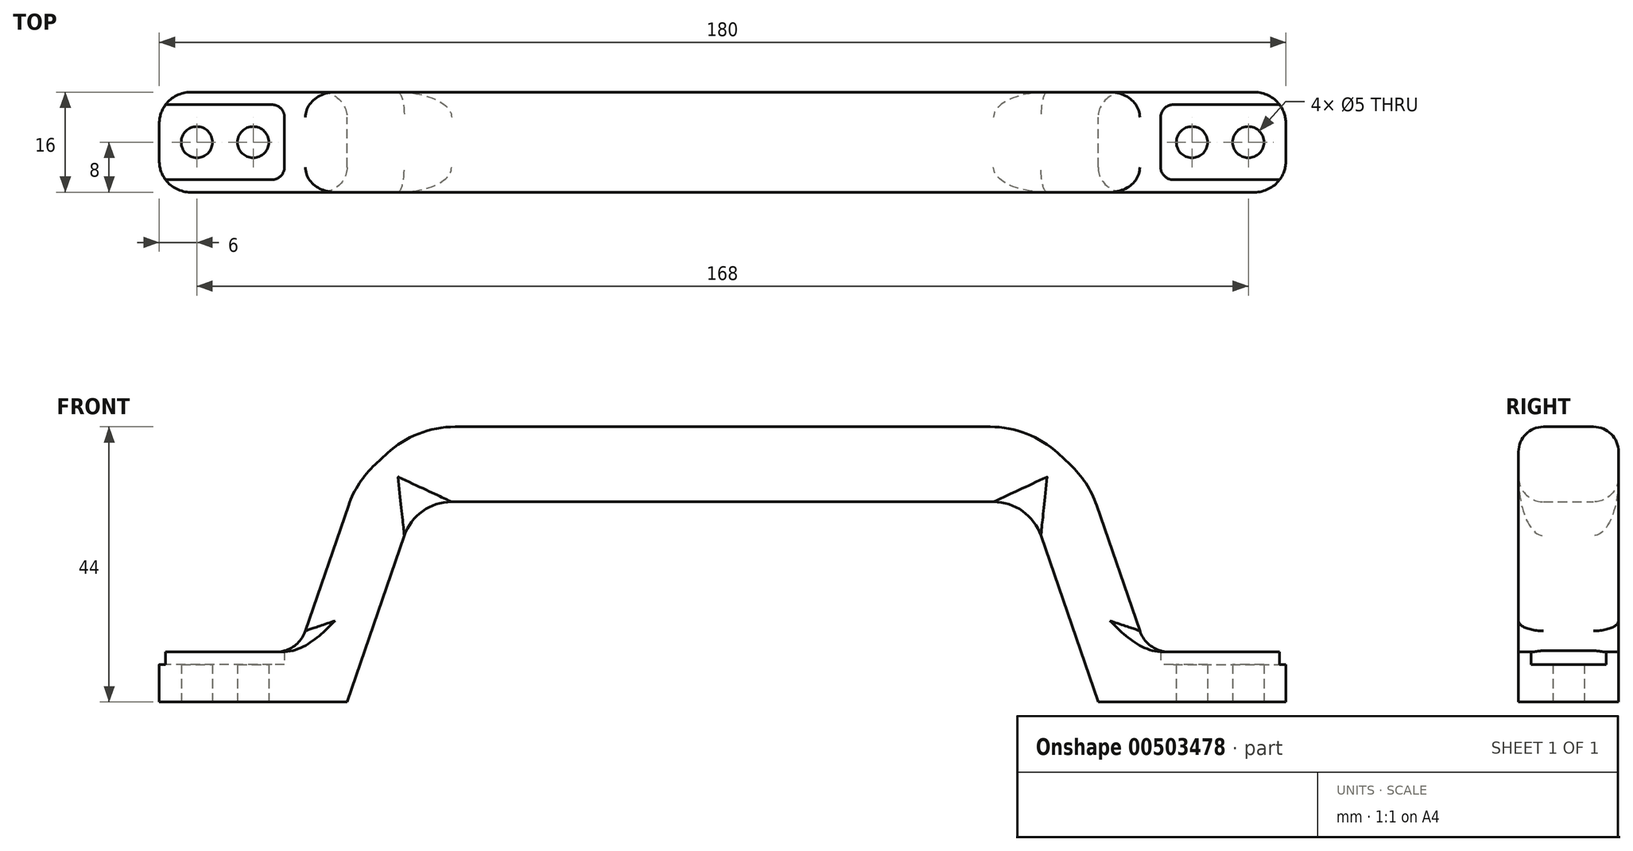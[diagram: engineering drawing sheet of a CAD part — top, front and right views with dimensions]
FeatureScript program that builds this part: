
annotation { "Feature Type Name" : "Feature", "Feature Type Description" : "" }
export const myFeature = defineFeature(function(context is Context, id is Id, definition is map)
    precondition{}
    {
        {
            var Q0;
            Q0=qCreatedBy(makeId("Front.planeOp"),FACE);
            var sketch = newSketch(context, id + "F0", { "sketchPlane" : qUnion([Q0])});
            skLineSegment(sketch, "E0", {"start": v(-60, 0) * mm, "end": v(-90, 0) * mm});
            skLineSegment(sketch, "E1", {"start": v(-90, 0) * mm, "end": v(-90, 8) * mm});
            skLineSegment(sketch, "E2", {"start": v(-90, 8) * mm, "end": v(-67.82, 8) * mm});
            skLineSegment(sketch, "E3", {"start": v(0, 0) * mm, "end": v(0, 32) * mm});
            skLineSegment(sketch, "E4", {"start": v(0, 32) * mm, "end": v(-49, 32) * mm});
            skLineSegment(sketch, "E5", {"start": v(-49, 32) * mm, "end": v(-60, 0) * mm});
            skLineSegment(sketch, "E6", {"start": v(0, 32) * mm, "end": v(0, 44) * mm});
            skLineSegment(sketch, "E7", {"start": v(0, 44) * mm, "end": v(-49, 44) * mm});
            skLineSegment(sketch, "E8.0", {"start": v(-58.46, 35.25) * mm, "end": v(-67.82, 8) * mm});
            skLineSegment(sketch, "E9", {"start": v(-58.46, 35.25) * mm, "end": v(-49, 44) * mm});
            skPoint(sketch, "E10.start.orphan", {"position": v(-60, 8) * mm});
            skSolve(sketch);
        }
        {
            var Q0;
            Q0 = qSketchRegion(id + "F0", true);
            extrude(context, id + "F1", {"entities" : qUnion([Q0]), "endBound" : BoundingType.SYMMETRIC, "depth" : 16 * mm, "offsetDistance" : 25 * mm});
        }
        {
            var Q0;
            Q0=qCreatedBy(makeId("Front.planeOp"),FACE);
            var sketch = newSketch(context, id + "F2", { "sketchPlane" : qUnion([Q0])});
            skLineSegment(sketch, "E11", {"start": v(0, 0) * mm, "end": v(-70, 0) * mm});
            skLineSegment(sketch, "E12", {"start": v(-70, 0) * mm, "end": v(-70, 6) * mm});
            skLineSegment(sketch, "E13", {"start": v(-70, 6) * mm, "end": v(-94, 6) * mm});
            skLineSegment(sketch, "E14", {"start": v(-94, 6) * mm, "end": v(-94, 12) * mm});
            skLineSegment(sketch, "E15", {"start": v(-94, 12) * mm, "end": v(-70, 12) * mm});
            skLineSegment(sketch, "E16", {"start": v(-70, 12) * mm, "end": v(-70, 6) * mm});
            skSolve(sketch);
        }
        {
            var Q0;
            Q0 = qSketchRegion(id + "F2", true);
            extrude(context, id + "F3", {"entities" : qUnion([Q0]), "endBound" : BoundingType.SYMMETRIC, "depth" : 12 * mm, "offsetDistance" : 25 * mm});
        }
        {
            var Q0;
            Q0=makeQuery(id+"F3.opExtrude","SWEPT_BODY",BODY,{"disambiguationData":[OSD([sQuery(id+"F2.wireOp",EDGE,"E13"),sQuery(id+"F2.wireOp",EDGE,"E14"),sQuery(id+"F2.wireOp",EDGE,"E15"),sQuery(id+"F2.wireOp",EDGE,"E16")])]});
            var Q1;
            Q1=makeQuery(id+"F1.opExtrude","SWEPT_BODY",BODY,{"disambiguationData":[OSD([sQuery(id+"F0.wireOp",EDGE,"E0"),sQuery(id+"F0.wireOp",EDGE,"E1"),sQuery(id+"F0.wireOp",EDGE,"E2"),sQuery(id+"F0.wireOp",EDGE,"E4"),sQuery(id+"F0.wireOp",EDGE,"E5"),sQuery(id+"F0.wireOp",EDGE,"E6"),sQuery(id+"F0.wireOp",EDGE,"E7"),sQuery(id+"F0.wireOp",EDGE,"E8.0"),sQuery(id+"F0.wireOp",EDGE,"E9")])]});
            booleanBodies(context, id + "F4", {"operationType" : BooleanOperationType.SUBTRACTION, "tools" : qUnion([Q0]), "targets" : qUnion([Q1])});
        }
        {
            var Q0;
            Q0=qCreatedBy(makeId("Top.planeOp"),FACE);
            var sketch = newSketch(context, id + "F5", { "sketchPlane" : qUnion([Q0])});
            skLineSegment(sketch, "E17", {"start": v(0, 0) * mm, "end": v(-75, 0) * mm});
            skLineSegment(sketch, "E18", {"start": v(-75, 0) * mm, "end": v(-84, 0) * mm});
            skCircle(sketch, "E19", {"center": v(-84, 0) * mm, "radius": 2.5 * mm});
            skCircle(sketch, "E20", {"center": v(-75, 0) * mm, "radius": 2.5 * mm});
            skSolve(sketch);
        }
        {
            var Q0;
            Q0 = qSketchRegion(id + "F5", true);
            extrude(context, id + "F6", {"entities" : qUnion([Q0]), "depth" : 25 * mm, "offsetDistance" : 25 * mm});
        }
        {
            var Q0;
            Q0=makeQuery(id+"F6.opExtrude","SWEPT_BODY",BODY,{"disambiguationData":[OSD([sQuery(id+"F5.wireOp",EDGE,"E19")])]});
            var Q1;
            Q1=makeQuery(id+"F6.opExtrude","SWEPT_BODY",BODY,{"disambiguationData":[OSD([sQuery(id+"F5.wireOp",EDGE,"E20")])]});
            var Q2;
            Q2=makeQuery(id+"F1.opExtrude","SWEPT_BODY",BODY,{"disambiguationData":[OSD([sQuery(id+"F0.wireOp",EDGE,"E0"),sQuery(id+"F0.wireOp",EDGE,"E1"),sQuery(id+"F0.wireOp",EDGE,"E2"),sQuery(id+"F0.wireOp",EDGE,"E4"),sQuery(id+"F0.wireOp",EDGE,"E5"),sQuery(id+"F0.wireOp",EDGE,"E6"),sQuery(id+"F0.wireOp",EDGE,"E7"),sQuery(id+"F0.wireOp",EDGE,"E8.0"),sQuery(id+"F0.wireOp",EDGE,"E9")])]});
            booleanBodies(context, id + "F7", {"operationType" : BooleanOperationType.SUBTRACTION, "tools" : qUnion([Q0, Q1]), "targets" : qUnion([Q2])});
        }
        {
            var Q0;
            Q0=makeQuery(id+"F1.opExtrude","CAP_EDGE",EDGE,{"disambiguationData":[OSD([sQuery(id+"F0.wireOp",EDGE,"E7")])],"isStart":false});
            var Q1;
            Q1=makeQuery(id+"F1.opExtrude","CAP_EDGE",EDGE,{"disambiguationData":[OSD([sQuery(id+"F0.wireOp",EDGE,"E9")])],"isStart":false});
            var Q2;
            Q2=makeQuery(id+"F1.opExtrude","CAP_EDGE",EDGE,{"disambiguationData":[OSD([sQuery(id+"F0.wireOp",EDGE,"E8.0")])],"isStart":false});
            var Q3;
            Q3=makeQuery(id+"F1.opExtrude","CAP_EDGE",EDGE,{"disambiguationData":[OSD([sQuery(id+"F0.wireOp",EDGE,"E8.0")])],"isStart":true});
            var Q4;
            Q4=makeQuery(id+"F1.opExtrude","CAP_EDGE",EDGE,{"disambiguationData":[OSD([sQuery(id+"F0.wireOp",EDGE,"E9")])],"isStart":true});
            var Q5;
            Q5=makeQuery(id+"F1.opExtrude","CAP_EDGE",EDGE,{"disambiguationData":[OSD([sQuery(id+"F0.wireOp",EDGE,"E7")])],"isStart":true});
            var Q6;
            Q6=makeQuery(id+"F1.opExtrude","CAP_EDGE",EDGE,{"disambiguationData":[OSD([sQuery(id+"F0.wireOp",EDGE,"E4")])],"isStart":false});
            var Q7;
            Q7=makeQuery(id+"F1.opExtrude","CAP_EDGE",EDGE,{"disambiguationData":[OSD([sQuery(id+"F0.wireOp",EDGE,"E5")])],"isStart":false});
            var Q8;
            Q8=makeQuery(id+"F1.opExtrude","CAP_EDGE",EDGE,{"disambiguationData":[OSD([sQuery(id+"F0.wireOp",EDGE,"E5")])],"isStart":true});
            var Q9;
            Q9=makeQuery(id+"F1.opExtrude","CAP_EDGE",EDGE,{"disambiguationData":[OSD([sQuery(id+"F0.wireOp",EDGE,"E4")])],"isStart":true});
            fillet(context, id + "F8", {"entities" : qUnion([Q0, Q1, Q2, Q3, Q4, Q5, Q6, Q7, Q8, Q9]), "radius" : 4 * mm, "tangentPropagation" : true, "allowEdgeOverflow" : false});
        }
        {
            var Q0;
            Q0=makeQuery(id+"F1.opExtrude","SWEPT_EDGE",EDGE,{"disambiguationData":[OSD([sQuery(id+"F0.wireOp",EDGE,"E8.0"),sQuery(id+"F0.wireOp",EDGE,"E9")])]});
            var Q1;
            Q1=makeQuery(id+"F1.opExtrude","SWEPT_EDGE",EDGE,{"disambiguationData":[OSD([sQuery(id+"F0.wireOp",EDGE,"E7"),sQuery(id+"F0.wireOp",EDGE,"E9")])]});
            fillet(context, id + "F9", {"entities" : qUnion([Q0, Q1]), "radius" : 16 * mm, "tangentPropagation" : true, "allowEdgeOverflow" : false});
        }
        {
            var Q0;
            Q0=makeQuery(id+"F1.opExtrude","SWEPT_EDGE",EDGE,{"disambiguationData":[OSD([sQuery(id+"F0.wireOp",EDGE,"E4"),sQuery(id+"F0.wireOp",EDGE,"E5")])]});
            fillet(context, id + "F10", {"entities" : qUnion([Q0]), "radius" : 8 * mm, "tangentPropagation" : true, "allowEdgeOverflow" : false});
        }
        {
            var Q0;
            Q0=makeQuery(id+"F1.opExtrude","CAP_EDGE",EDGE,{"disambiguationData":[OSD([sQuery(id+"F0.wireOp",EDGE,"E1")])],"isStart":false});
            var Q1;
            Q1=makeQuery(id+"F1.opExtrude","CAP_EDGE",EDGE,{"disambiguationData":[OSD([sQuery(id+"F0.wireOp",EDGE,"E1")])],"isStart":true});
            fillet(context, id + "F11", {"entities" : qUnion([Q0, Q1]), "radius" : 5 * mm, "tangentPropagation" : true, "allowEdgeOverflow" : false});
        }
        {
            var Q0;
            Q0=makeQuery(id+"F4.opBoolean","COPY",EDGE,{"derivedFrom":makeQuery(id+"F3.opExtrude","CAP_EDGE",EDGE,{"disambiguationData":[OSD([sQuery(id+"F2.wireOp",EDGE,"E16")])],"isStart":true})});
            var Q1;
            Q1=makeQuery(id+"F4.opBoolean","COPY",EDGE,{"derivedFrom":makeQuery(id+"F3.opExtrude","CAP_EDGE",EDGE,{"disambiguationData":[OSD([sQuery(id+"F2.wireOp",EDGE,"E16")])],"isStart":false})});
            fillet(context, id + "F12", {"entities" : qUnion([Q0, Q1]), "radius" : 2 * mm, "tangentPropagation" : true, "allowEdgeOverflow" : false});
        }
        {
            var Q0;
            Q0=makeQuery(id+"F1.opExtrude","SWEPT_EDGE",EDGE,{"disambiguationData":[OSD([sQuery(id+"F0.wireOp",EDGE,"E2"),sQuery(id+"F0.wireOp",EDGE,"E8.0")])]});
            fillet(context, id + "F13", {"entities" : qUnion([Q0]), "radius" : 5 * mm, "tangentPropagation" : true, "allowEdgeOverflow" : false});
        }
        {
            var Q0;
            Q0=makeQuery(id+"F1.opExtrude","SWEPT_BODY",BODY,{"disambiguationData":[OSD([sQuery(id+"F0.wireOp",EDGE,"E0"),sQuery(id+"F0.wireOp",EDGE,"E1"),sQuery(id+"F0.wireOp",EDGE,"E2"),sQuery(id+"F0.wireOp",EDGE,"E4"),sQuery(id+"F0.wireOp",EDGE,"E5"),sQuery(id+"F0.wireOp",EDGE,"E6"),sQuery(id+"F0.wireOp",EDGE,"E7"),sQuery(id+"F0.wireOp",EDGE,"E8.0"),sQuery(id+"F0.wireOp",EDGE,"E9")])]});
            var Q1;
            Q1=qCreatedBy(makeId("Right.planeOp"),FACE);
            mirror(context, id + "F14", {"operationType" : NewBodyOperationType.ADD, "entities" : qUnion([Q0]), "mirrorPlane" : qUnion([Q1])});
        }
    });
